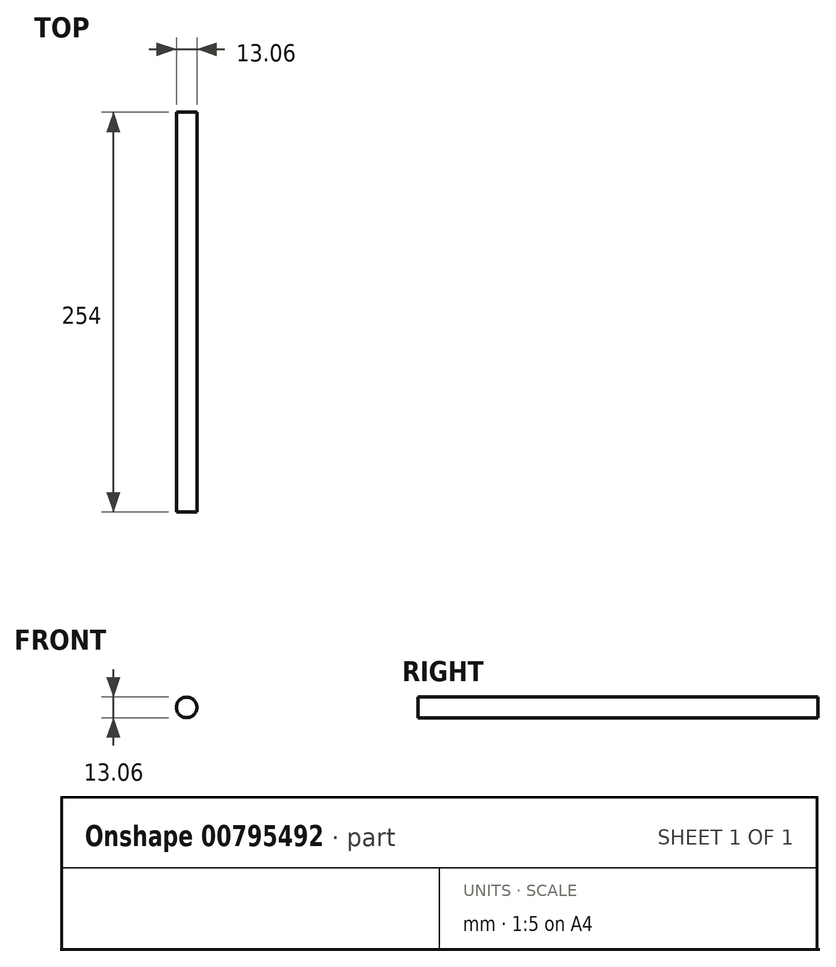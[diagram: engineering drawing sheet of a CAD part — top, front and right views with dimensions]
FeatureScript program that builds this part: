
annotation { "Feature Type Name" : "Feature", "Feature Type Description" : "" }
export const myFeature = defineFeature(function(context is Context, id is Id, definition is map)
    precondition{}
    {
        {
            var Q0;
            Q0=qCreatedBy(makeId("Top.planeOp"),FACE);
            var sketch = newSketch(context, id + "F0", { "sketchPlane" : qUnion([Q0])});
            skCircle(sketch, "E0", {"center": v(-30.38, 35.5) * mm, "radius": 13.36 * mm});
            skPoint(sketch, "E0.first.point", {"position": v(-34.52, 48.2) * mm});
            skPoint(sketch, "E0.second.point", {"position": v(-33.46, 22.5) * mm});
            skPoint(sketch, "E0.third.point", {"position": v(-17.03, 36) * mm});
            skSolve(sketch);
        }
        {
            var Q0;
            Q0 = qSketchRegion(id + "F0", true);
            extrude(context, id + "F1", {"entities" : qUnion([Q0]), "endBound" : BoundingType.SYMMETRIC, "depth" : 254 * mm, "offsetDistance" : 25.4 * mm});
        }
        {
            var Q0;
            Q0=makeQuery(id+"F1.opExtrude","SWEPT_BODY",BODY,{"disambiguationData":[OSD([sQuery(id+"F0.wireOp",EDGE,"E0")])]});
            deleteBodies(context, id + "F2", {"entities" : qUnion([Q0])});
        }
        {
            var Q0;
            Q0=qCreatedBy(makeId("Top.planeOp"),FACE);
            var sketch = newSketch(context, id + "F3", { "sketchPlane" : qUnion([Q0])});
            skCircle(sketch, "E1", {"center": v(-33.73, 38.47) * mm, "radius": 6.35 * mm});
            skPoint(sketch, "E1.first.point", {"position": v(-37.73, 43.4) * mm});
            skPoint(sketch, "E1.second.point", {"position": v(-28.68, 34.62) * mm});
            skPoint(sketch, "E1.third.point", {"position": v(-37.87, 33.66) * mm});
            skSolve(sketch);
        }
        {
            var Q0;
            Q0 = qSketchRegion(id + "F3", true);
            extrude(context, id + "F4", {"entities" : qUnion([Q0]), "endBound" : BoundingType.SYMMETRIC, "depth" : 254 * mm, "offsetDistance" : 25.4 * mm});
        }
        {
            var Q0;
            Q0=makeQuery(id+"F4.opExtrude","SWEPT_BODY",BODY,{"disambiguationData":[OSD([sQuery(id+"F3.wireOp",EDGE,"E1")])]});
            deleteBodies(context, id + "F5", {"entities" : qUnion([Q0])});
        }
        {
            var Q0;
            Q0=qCreatedBy(makeId("Front.planeOp"),FACE);
            var sketch = newSketch(context, id + "F6", { "sketchPlane" : qUnion([Q0])});
            skCircle(sketch, "E2", {"center": v(-33.63, 30.98) * mm, "radius": 6.53 * mm});
            skPoint(sketch, "E2.first.point", {"position": v(-35.15, 37.33) * mm});
            skPoint(sketch, "E2.second.point", {"position": v(-27.18, 29.99) * mm});
            skPoint(sketch, "E2.third.point", {"position": v(-39.13, 27.47) * mm});
            skSolve(sketch);
        }
        {
            var Q0;
            Q0 = qSketchRegion(id + "F6", true);
            extrude(context, id + "F7", {"entities" : qUnion([Q0]), "endBound" : BoundingType.SYMMETRIC, "depth" : 254 * mm, "offsetDistance" : 25.4 * mm});
        }
    });
